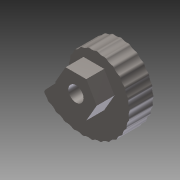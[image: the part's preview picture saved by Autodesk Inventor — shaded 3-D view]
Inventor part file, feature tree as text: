
AUTODESK INVENTOR PART (.ipt)
format: ipt  version: 2016 (Build 200138000, 138)  size: 181,760 bytes
history: native  units: in
note: dims shown in document units (in); Inventor stores cm internally (conversion verified against a paired STEP export)
features: fillet x1, other x1, imported_body x1
ambient origin geometry x8: Origin, YZ Plane, XZ Plane, XY Plane, X Axis, Y Axis, Z Axis, Center Point
bodies: Body1 (feature_tree)
feature tree (3):
  fillet  "Fillet1"  [1 undecoded]
  other  "217-3431-STEP1"
  imported_body  "Base1"
note: 1 required parameter value undecoded (feature->parameter linkage not recoverable at this tier; creation-order binding heuristic only, values carry confidence <= 0.55)
